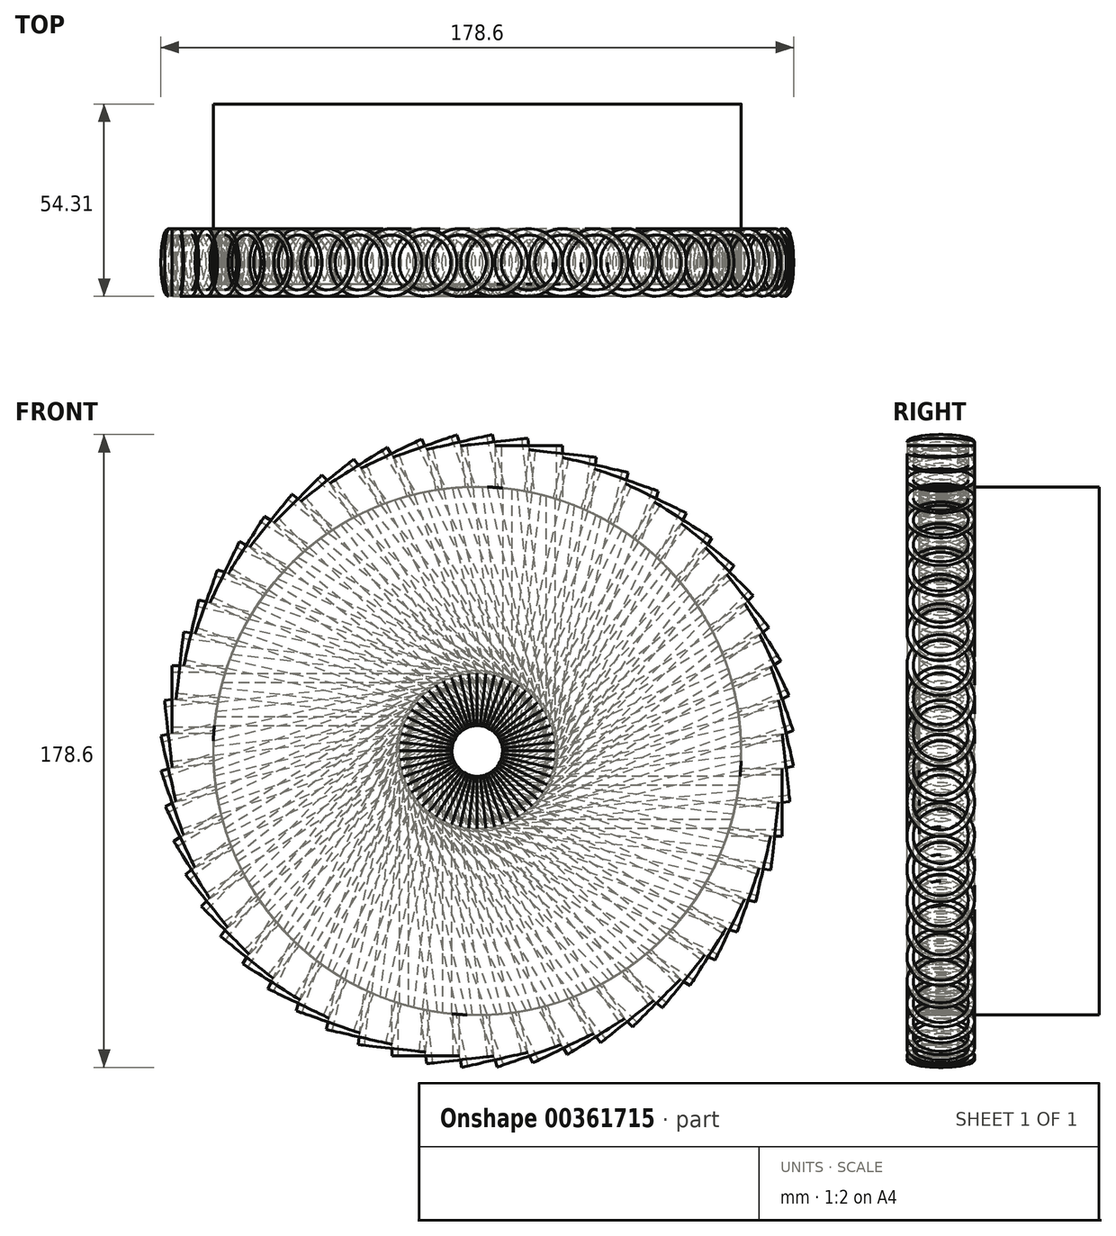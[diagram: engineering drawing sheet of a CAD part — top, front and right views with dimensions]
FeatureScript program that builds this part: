
annotation { "Feature Type Name" : "Feature", "Feature Type Description" : "" }
export const myFeature = defineFeature(function(context is Context, id is Id, definition is map)
    precondition{}
    {
        {
            var Q0;
            Q0=qCreatedBy(makeId("Front.planeOp"),FACE);
            var sketch = newSketch(context, id + "F0", { "sketchPlane" : qUnion([Q0])});
            skCircle(sketch, "E0", {"center": v(0, 0) * mm, "radius": 74.54 * mm});
            skSolve(sketch);
        }
        {
            var Q0;
            Q0 = qSketchRegion(id + "F0", true);
            extrude(context, id + "F1", {"entities" : qUnion([Q0]), "depth" : 27.94 * mm});
        }
        {
            var Q0;
            Q0=makeQuery(id+"F0.imprint","IMPRINT",FACE,{"disambiguationData":[TD([[makeQuery(id+"F0.imprint","IMPRINT",EDGE,{"derivedFrom":sQuery(id+"F0.wireOp",EDGE,"E0")}),1.0]])]});
            extrude(context, id + "F2", {"entities" : qUnion([Q0]), "operationType" : NewBodyOperationType.ADD, "depth" : 49.53 * mm});
        }
        {
            var Q0;
            Q0 = qSketchRegion(id + "F0", true);
            extrude(context, id + "F3", {"entities" : qUnion([Q0]), "operationType" : NewBodyOperationType.ADD, "oppositeDirection" : true, "depth" : 1.27 * mm});
        }
        {
            var Q0;
            Q0=qCreatedBy(makeId("Top.planeOp"),FACE);
            var sketch = newSketch(context, id + "F4", { "sketchPlane" : qUnion([Q0])});
            skCircle(sketch, "E1", {"center": v(-14.53, -43.48) * mm, "radius": 7.76 * mm});
            skCircle(sketch, "E2", {"center": v(-14.53, -43.48) * mm, "radius": 9.55 * mm});
            skSolve(sketch);
        }
        {
            var Q0;
            Q0 = qSketchRegion(id + "F4", true);
            extrude(context, id + "F5", {"entities" : qUnion([Q0]), "operationType" : NewBodyOperationType.ADD, "oppositeDirection" : true, "depth" : 86.1 * mm});
        }
        {
            var Q0;
            Q0=makeQuery(id+"F1.opExtrude","SWEPT_BODY",BODY,{"disambiguationData":[OSD([sQuery(id+"F0.wireOp",EDGE,"E0")])]});
            var Q1;
            {var subQ0=sQuery(id+"F0.wireOp",EDGE,"E0");Q1=makeQuery(id+"F5.boolean.opBoolean","SPLIT",FACE,{"disambiguationData":[TD([makeQuery(id+"F3.opExtrude","CAP_FACE",FACE,{"disambiguationData":[OSD([subQ0])],"isStart":false})])],"derivedFrom":makeQuery(id+"F3.boolean.opBoolean","MERGE",FACE,{"derivedFrom":[makeQuery(id+"F2.boolean.opBoolean","MERGE",FACE,{"derivedFrom":[makeQuery(id+"F1.opExtrude","SWEPT_FACE",FACE,{"disambiguationData":[OSD([subQ0])]}),makeQuery(id+"F2.opExtrude","SWEPT_FACE",FACE,{"disambiguationData":[OSD([subQ0])]})]}),makeQuery(id+"F3.opExtrude","SWEPT_FACE",FACE,{"disambiguationData":[OSD([subQ0])]})]})});}
            circularPattern(context, id + "F6", {"entities" : qUnion([Q0]), "axis" : qUnion([Q1]), "angle" : 360 * degree, "instanceCount" : 4, "equalSpace" : true});
        }
        {
            var Q0;
            Q0=makeQuery(id+"F1.opExtrude","SWEPT_BODY",BODY,{"disambiguationData":[OSD([sQuery(id+"F0.wireOp",EDGE,"E0")])]});
            var Q1;
            {var subQ0=sQuery(id+"F0.wireOp",EDGE,"E0");Q1=makeQuery(id+"F5.boolean.opBoolean","SPLIT",FACE,{"disambiguationData":[TD([makeQuery(id+"F3.opExtrude","CAP_FACE",FACE,{"disambiguationData":[OSD([subQ0])],"isStart":false})])],"derivedFrom":makeQuery(id+"F3.boolean.opBoolean","MERGE",FACE,{"derivedFrom":[makeQuery(id+"F2.boolean.opBoolean","MERGE",FACE,{"derivedFrom":[makeQuery(id+"F1.opExtrude","SWEPT_FACE",FACE,{"disambiguationData":[OSD([subQ0])]}),makeQuery(id+"F2.opExtrude","SWEPT_FACE",FACE,{"disambiguationData":[OSD([subQ0])]})]}),makeQuery(id+"F3.opExtrude","SWEPT_FACE",FACE,{"disambiguationData":[OSD([subQ0])]})]})});}
            circularPattern(context, id + "F7", {"entities" : qUnion([Q0]), "axis" : qUnion([Q1]), "angle" : 360 * degree, "instanceCount" : 56, "equalSpace" : true});
        }
    });
